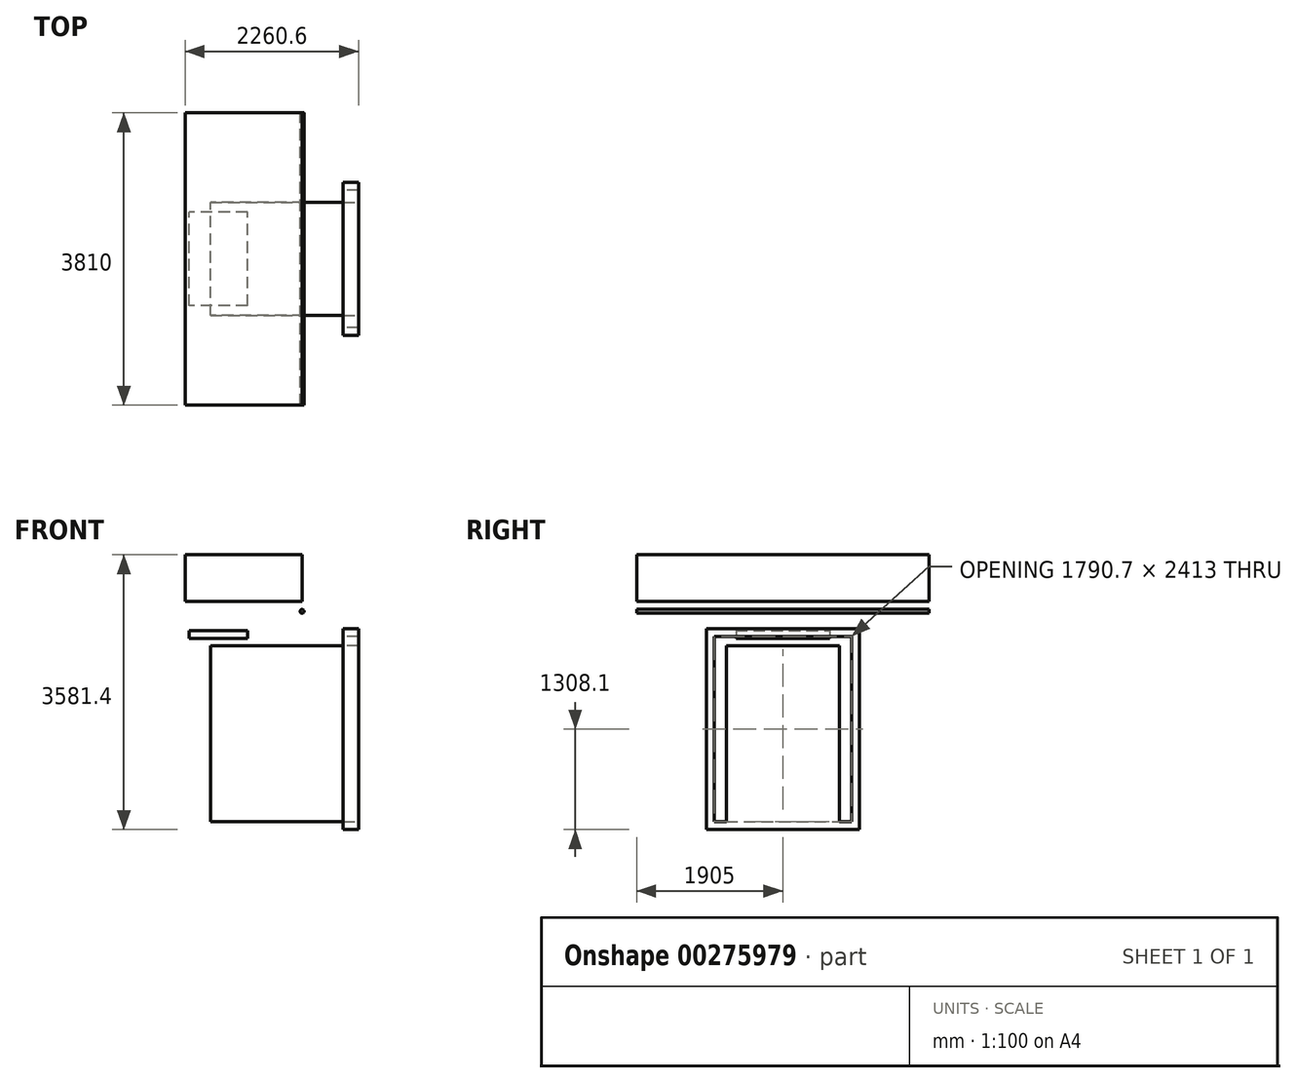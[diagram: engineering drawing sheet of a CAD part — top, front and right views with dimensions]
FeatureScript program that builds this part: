
annotation { "Feature Type Name" : "Feature", "Feature Type Description" : "" }
export const myFeature = defineFeature(function(context is Context, id is Id, definition is map)
    precondition{}
    {
        {
            var Q0;
            Q0=qCreatedBy(makeId("Right.planeOp"),FACE);
            var sketch = newSketch(context, id + "F0", { "sketchPlane" : qUnion([Q0])});
            skLineSegment(sketch, "E0.bottom", {"start": v(-895.35, 1206.5) * mm, "end": v(895.35, 1206.5) * mm});
            skLineSegment(sketch, "E0.top", {"start": v(-895.35, -1206.5) * mm, "end": v(895.35, -1206.5) * mm});
            skLineSegment(sketch, "E0.left", {"start": v(-895.35, 1206.5) * mm, "end": v(-895.35, -1206.5) * mm});
            skLineSegment(sketch, "E0.right", {"start": v(895.35, 1206.5) * mm, "end": v(895.35, -1206.5) * mm});
            skLineSegment(sketch, "E1.bottom", {"start": v(-996.95, 1308.1) * mm, "end": v(996.95, 1308.1) * mm});
            skLineSegment(sketch, "E1.top", {"start": v(-996.95, -1308.1) * mm, "end": v(996.95, -1308.1) * mm});
            skLineSegment(sketch, "E1.left", {"start": v(-996.95, 1308.1) * mm, "end": v(-996.95, -1308.1) * mm});
            skLineSegment(sketch, "E1.right", {"start": v(996.95, 1308.1) * mm, "end": v(996.95, -1308.1) * mm});
            skSolve(sketch);
        }
        {
            var Q0;
            Q0=qSketchRegion(id+"F0",true);
            extrude(context, id + "F1", {"entities" : qUnion([Q0]), "depth" : 203.2 * mm});
        }
        {
            var Q0;
            Q0=makeQuery(id+"F1.opExtrude","CAP_FACE",FACE,{"disambiguationData":[OSD([sQuery(id+"F0.wireOp",EDGE,"E0.bottom"),sQuery(id+"F0.wireOp",EDGE,"E0.top"),sQuery(id+"F0.wireOp",EDGE,"E0.left"),sQuery(id+"F0.wireOp",EDGE,"E0.right"),sQuery(id+"F0.wireOp",EDGE,"E1.bottom"),sQuery(id+"F0.wireOp",EDGE,"E1.top"),sQuery(id+"F0.wireOp",EDGE,"E1.left"),sQuery(id+"F0.wireOp",EDGE,"E1.right")])],"isStart":true});
            cPlane(context, id + "F2", {"entities" : qUnion([Q0]), "cplaneType" : CPlaneType.OFFSET, "offset" : 533.4 * mm, "width" : 152.4 * mm, "height" : 152.4 * mm});
        }
        {
            var Q0;
            Q0=qCreatedBy(id+"F2.planeOp",FACE);
            var sketch = newSketch(context, id + "F3", { "sketchPlane" : qUnion([Q0])});
            skLineSegment(sketch, "E2.bottom", {"start": v(-1905, 2273.3) * mm, "end": v(1905, 2273.3) * mm});
            skLineSegment(sketch, "E2.top", {"start": v(-1905, 1663.7) * mm, "end": v(1905, 1663.7) * mm});
            skLineSegment(sketch, "E2.left", {"start": v(-1905, 2273.3) * mm, "end": v(-1905, 1663.7) * mm});
            skLineSegment(sketch, "E2.right", {"start": v(1905, 2273.3) * mm, "end": v(1905, 1663.7) * mm});
            skSolve(sketch);
        }
        {
            var Q0;
            Q0=makeQuery(id+"F3.imprint","IMPRINT",FACE,{"disambiguationData":[TD([[makeQuery(id+"F3.imprint","IMPRINT",EDGE,{"derivedFrom":sQuery(id+"F3.wireOp",EDGE,"E2.bottom")}),-1.0]])]});
            extrude(context, id + "F4", {"entities" : qUnion([Q0]), "depth" : 1524 * mm});
        }
        {
            var Q0;
            Q0=qCreatedBy(makeId("Front.planeOp"),FACE);
            var sketch = newSketch(context, id + "F5", { "sketchPlane" : qUnion([Q0])});
            skCircle(sketch, "E3", {"center": v(-533.4, 1536.7) * mm, "radius": 25.4 * mm});
            skSolve(sketch);
        }
        {
            var Q0;
            Q0=makeQuery(id+"F5.imprint","IMPRINT",FACE,{"disambiguationData":[TD([[makeQuery(id+"F5.imprint","IMPRINT",EDGE,{"derivedFrom":sQuery(id+"F5.wireOp",EDGE,"E3")}),1.0]])]});
            extrude(context, id + "F6", {"entities" : qUnion([Q0]), "depth" : 1905 * mm, "hasSecondDirection" : true, "secondDirectionOppositeDirection" : true, "secondDirectionDepth" : 1905 * mm});
        }
        {
            var Q0;
            Q0=qCreatedBy(makeId("Front.planeOp"),FACE);
            var sketch = newSketch(context, id + "F7", { "sketchPlane" : qUnion([Q0])});
            skLineSegment(sketch, "E4.bottom", {"start": v(-1244.6, 1282.7) * mm, "end": v(-2006.6, 1282.7) * mm});
            skLineSegment(sketch, "E4.top", {"start": v(-1244.6, 1181.1) * mm, "end": v(-2006.6, 1181.1) * mm});
            skLineSegment(sketch, "E4.left", {"start": v(-1244.6, 1282.7) * mm, "end": v(-1244.6, 1181.1) * mm});
            skLineSegment(sketch, "E4.right", {"start": v(-2006.6, 1282.7) * mm, "end": v(-2006.6, 1181.1) * mm});
            skSolve(sketch);
        }
        {
            var Q0;
            Q0=makeQuery(id+"F7.imprint","IMPRINT",FACE,{"disambiguationData":[TD([[makeQuery(id+"F7.imprint","IMPRINT",EDGE,{"derivedFrom":sQuery(id+"F7.wireOp",EDGE,"E4.bottom")}),1.0]])]});
            extrude(context, id + "F8", {"entities" : qUnion([Q0]), "depth" : 609.6 * mm, "hasSecondDirection" : true, "secondDirectionOppositeDirection" : true, "secondDirectionDepth" : 609.6 * mm});
        }
        {
            var Q0;
            Q0=qCreatedBy(makeId("Front.planeOp"),FACE);
            var sketch = newSketch(context, id + "F9", { "sketchPlane" : qUnion([Q0])});
            skLineSegment(sketch, "E5", {"start": v(203.2, 1088.39) * mm, "end": v(-1727.2, 1088.39) * mm});
            skLineSegment(sketch, "E6", {"start": v(-1727.2, 1088.39) * mm, "end": v(-1727.2, -1206.5) * mm});
            skLineSegment(sketch, "E7", {"start": v(-1727.2, -1206.5) * mm, "end": v(203.2, -1206.5) * mm});
            skLineSegment(sketch, "E8", {"start": v(203.2, -1206.5) * mm, "end": v(203.2, 1088.39) * mm});
            skSolve(sketch);
        }
        {
            var Q0;
            Q0=makeQuery(id+"F9.imprint","IMPRINT",FACE,{"disambiguationData":[TD([[makeQuery(id+"F9.imprint","IMPRINT",EDGE,{"derivedFrom":sQuery(id+"F9.wireOp",EDGE,"E5")}),1.0]])]});
            extrude(context, id + "F10", {"entities" : qUnion([Q0]), "operationType" : NewBodyOperationType.ADD, "depth" : 736.6 * mm, "hasSecondDirection" : true, "secondDirectionOppositeDirection" : true, "secondDirectionDepth" : 736.6 * mm});
        }
    });
